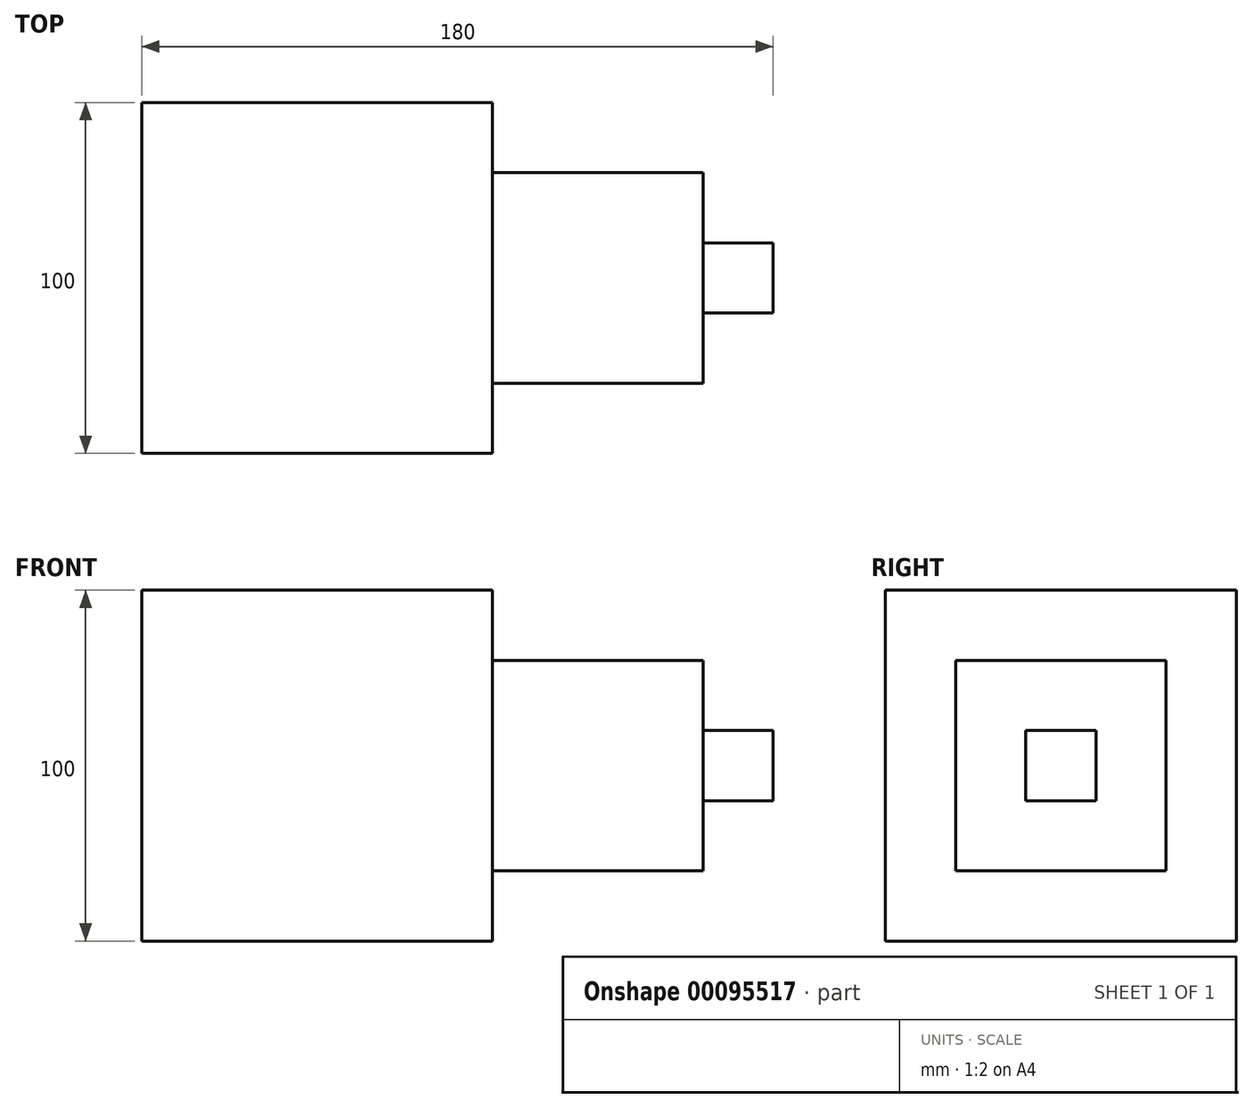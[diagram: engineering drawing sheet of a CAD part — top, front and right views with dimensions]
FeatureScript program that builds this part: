
annotation { "Feature Type Name" : "Feature", "Feature Type Description" : "" }
export const myFeature = defineFeature(function(context is Context, id is Id, definition is map)
    precondition{}
    {
        {
            var Q0;
            Q0=qCreatedBy(makeId("Right.planeOp"),FACE);
            var sketch = newSketch(context, id + "F0", { "sketchPlane" : qUnion([Q0])});
            skLineSegment(sketch, "E0.bottom", {"start": v(-50.46, -53.98) * mm, "end": v(49.54, -53.98) * mm});
            skLineSegment(sketch, "E0.top", {"start": v(-50.46, 46.02) * mm, "end": v(49.54, 46.02) * mm});
            skLineSegment(sketch, "E0.left", {"start": v(-50.46, -53.98) * mm, "end": v(-50.46, 46.02) * mm});
            skLineSegment(sketch, "E0.right", {"start": v(49.54, -53.98) * mm, "end": v(49.54, 46.02) * mm});
            skSolve(sketch);
        }
        {
            var Q0;
            Q0=makeQuery(id+"F0.imprint","IMPRINT",FACE,{"disambiguationData":[TD([[makeQuery(id+"F0.imprint","IMPRINT",EDGE,{"derivedFrom":sQuery(id+"F0.wireOp",EDGE,"E0.bottom")}),1.0]])]});
            extrude(context, id + "F1", {"entities" : qUnion([Q0]), "depth" : 100 * mm});
        }
        {
            var Q0;
            Q0=makeQuery(id+"F1.opExtrude","CAP_FACE",FACE,{"disambiguationData":[OSD([sQuery(id+"F0.wireOp",EDGE,"E0.bottom"),sQuery(id+"F0.wireOp",EDGE,"E0.top"),sQuery(id+"F0.wireOp",EDGE,"E0.left"),sQuery(id+"F0.wireOp",EDGE,"E0.right")])],"isStart":false});
            var sketch = newSketch(context, id + "F2", { "sketchPlane" : qUnion([Q0])});
            skLineSegment(sketch, "E1.bottom", {"start": v(-30.46, 26.02) * mm, "end": v(29.54, 26.02) * mm});
            skLineSegment(sketch, "E1.top", {"start": v(-30.46, -33.98) * mm, "end": v(29.54, -33.98) * mm});
            skLineSegment(sketch, "E1.left", {"start": v(-30.46, 26.02) * mm, "end": v(-30.46, -33.98) * mm});
            skLineSegment(sketch, "E1.right", {"start": v(29.54, 26.02) * mm, "end": v(29.54, -33.98) * mm});
            skSolve(sketch);
        }
        {
            var Q0;
            Q0=makeQuery(id+"F2.imprint","IMPRINT",FACE,{"disambiguationData":[TD([[makeQuery(id+"F2.imprint","IMPRINT",EDGE,{"derivedFrom":sQuery(id+"F2.wireOp",EDGE,"E1.bottom")}),-1.0]])]});
            extrude(context, id + "F3", {"entities" : qUnion([Q0]), "operationType" : NewBodyOperationType.ADD, "depth" : 60 * mm});
        }
        {
            var Q0;
            Q0=makeQuery(id+"F3.opExtrude","CAP_FACE",FACE,{"disambiguationData":[OSD([sQuery(id+"F2.wireOp",EDGE,"E1.bottom"),sQuery(id+"F2.wireOp",EDGE,"E1.top"),sQuery(id+"F2.wireOp",EDGE,"E1.left"),sQuery(id+"F2.wireOp",EDGE,"E1.right")])],"isStart":false});
            var sketch = newSketch(context, id + "F4", { "sketchPlane" : qUnion([Q0])});
            skLineSegment(sketch, "E2.bottom", {"start": v(9.54, -13.98) * mm, "end": v(-10.46, -13.98) * mm});
            skLineSegment(sketch, "E2.top", {"start": v(9.54, 6.02) * mm, "end": v(-10.46, 6.02) * mm});
            skLineSegment(sketch, "E2.left", {"start": v(9.54, -13.98) * mm, "end": v(9.54, 6.02) * mm});
            skLineSegment(sketch, "E2.right", {"start": v(-10.46, -13.98) * mm, "end": v(-10.46, 6.02) * mm});
            skSolve(sketch);
        }
        {
            var Q0;
            Q0=makeQuery(id+"F4.imprint","IMPRINT",FACE,{"disambiguationData":[TD([[makeQuery(id+"F4.imprint","IMPRINT",EDGE,{"derivedFrom":sQuery(id+"F4.wireOp",EDGE,"E2.bottom")}),-1.0]])]});
            extrude(context, id + "F5", {"entities" : qUnion([Q0]), "operationType" : NewBodyOperationType.ADD, "depth" : 20 * mm});
        }
    });
